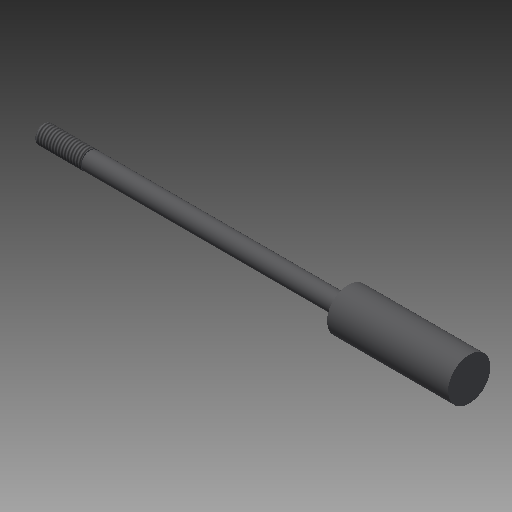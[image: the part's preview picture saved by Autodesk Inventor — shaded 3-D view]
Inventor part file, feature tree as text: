
AUTODESK INVENTOR PART (.ipt)
format: ipt  version: 2017 (Build 210142000, 142)  size: 141,824 bytes
history: native  units: in
note: dims shown in document units (in); Inventor stores cm internally (conversion verified against a paired STEP export)
features: other x70, revolve x3, sketch x3, thread x1
ambient origin geometry x8: Origin, YZ Plane, XZ Plane, XY Plane, X Axis, Y Axis, Z Axis, Center Point
bodies: Solid1 (feature_tree)
feature tree (77):
  revolve  "Revolution1"  Angle=360.0deg
  revolve  "Revolution2"  Angle=360.0deg
  thread  "Thread1"  [1 undecoded]
  revolve  "Revolution3"  [1 undecoded]
  other  "dia1_XY"
  other  "dia1_YZ"
  other  "dia1_ZX"
  other  "dia1_X"
  other  "dia1_Y"
  other  "dia1_Z"
  other  "dia1_Center"
  other  "dia12_XY"
  other  "dia12_YZ"
  other  "dia12_ZX"
  other  "dia12_X"
  other  "dia12_Y"
  other  "dia12_Z"
  other  "dia12_Center"
  other  "dia2_XY"
  other  "dia2_YZ"
  other  "dia2_ZX"
  other  "dia2_X"
  other  "dia2_Y"
  other  "dia2_Z"
  other  "dia2_Center"
  other  "dia22_XY"
  other  "dia22_YZ"
  other  "dia22_ZX"
  other  "dia22_X"
  other  "dia22_Y"
  other  "dia22_Z"
  other  "dia22_Center"
  other  "rl1_XY"
  other  "rl1_YZ"
  other  "rl1_ZX"
  other  "rl1_X"
  other  "rl1_Y"
  other  "rl1_Z"
  other  "rl1_Center"
  other  "rl2_XY"
  other  "rl2_YZ"
  other  "rl2_ZX"
  other  "rl2_X"
  other  "rl2_Y"
  other  "rl2_Z"
  other  "rl2_Center"
  other  "rod_cp_XY"
  other  "rod_cp_YZ"
  other  "rod_cp_ZX"
  other  "rod_cp_X"
  other  "rod_cp_Y"
  other  "rod_cp_Z"
  other  "rod_cp_Center"
  other  "thd1_XY"
  other  "thd1_YZ"
  other  "thd1_ZX"
  other  "thd1_X"
  other  "thd1_Y"
  other  "thd1_Z"
  other  "thd1_Center"
  other  "thd2_XY"
  other  "thd2_YZ"
  other  "thd2_ZX"
  other  "thd2_X"
  other  "thd2_Y"
  other  "thd2_Z"
  other  "thd2_Center"
  other  "to_rod_clevis_XY"
  other  "to_rod_clevis_YZ"
  other  "to_rod_clevis_ZX"
  other  "to_rod_clevis_X"
  other  "to_rod_clevis_Y"
  other  "to_rod_clevis_Z"
  other  "to_rod_clevis_Center"
  sketch  "Sketch_1"  dims[d0=360.0deg d1=360.0deg]
  sketch  "Sketch_3"  dims[d2=0.4814in d3=0.0in d4=360.0deg d5=0.0in d6=0.0in d7=0.0in d8=0.0in]
  sketch  "Sketch_30"
note: 2 required parameter values undecoded (feature->parameter linkage not recoverable at this tier; creation-order binding heuristic only, values carry confidence <= 0.55)
